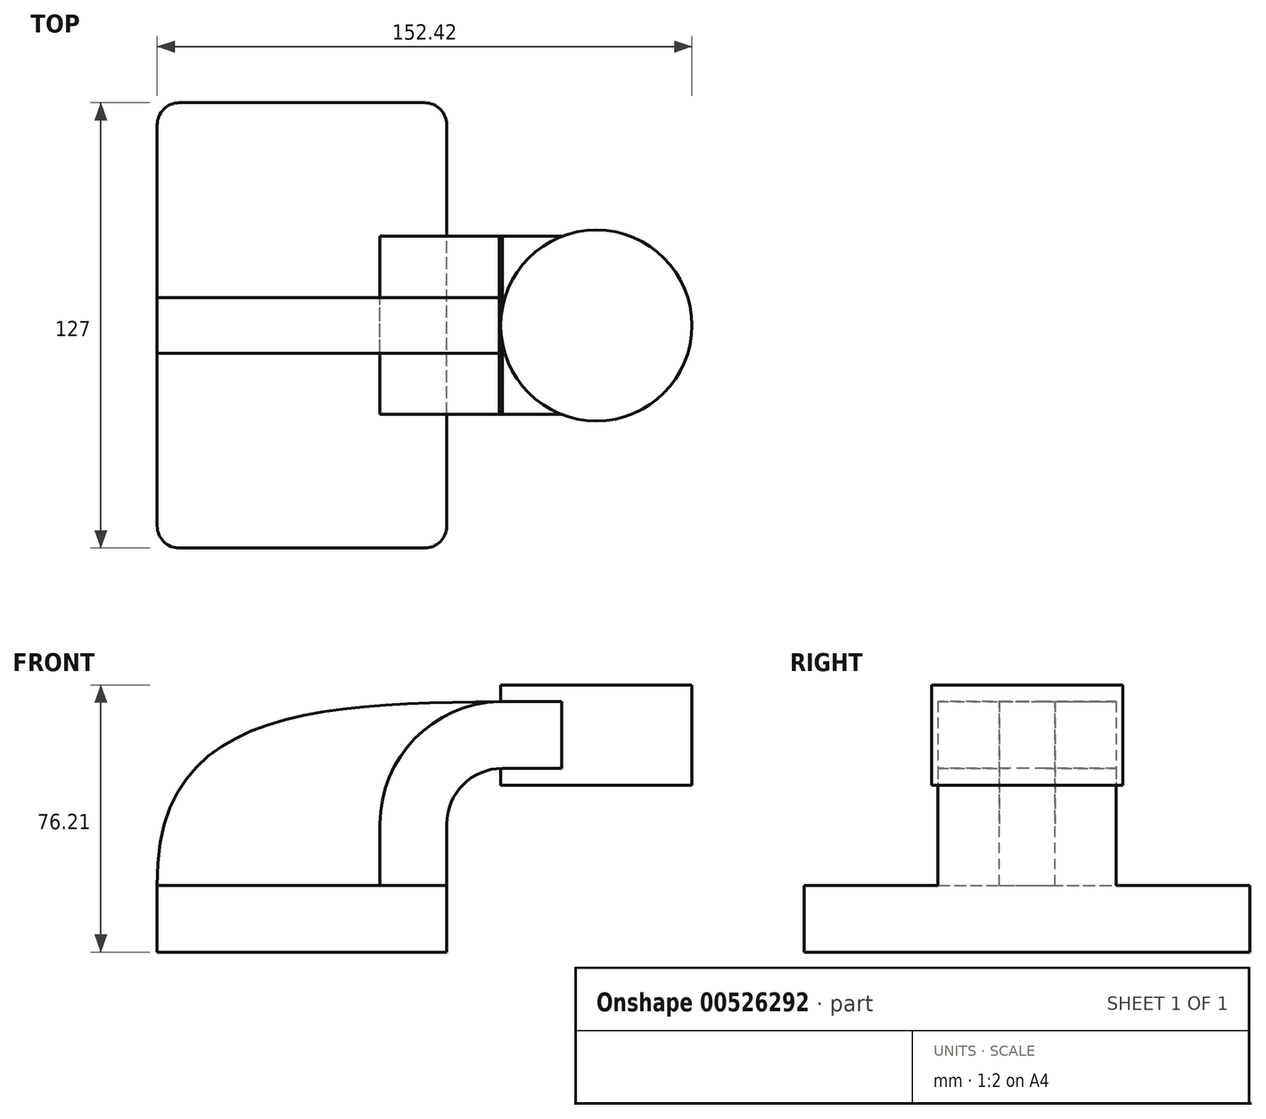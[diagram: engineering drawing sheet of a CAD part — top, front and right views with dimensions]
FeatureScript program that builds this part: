
annotation { "Feature Type Name" : "Feature", "Feature Type Description" : "" }
export const myFeature = defineFeature(function(context is Context, id is Id, definition is map)
    precondition{}
    {
        {
            var Q0;
            Q0=qCreatedBy(makeId("Front.planeOp"),FACE);
            var sketch = newSketch(context, id + "F0", { "sketchPlane" : qUnion([Q0])});
            skLineSegment(sketch, "E0.bottom", {"start": v(-41.28, 9.52) * mm, "end": v(41.27, 9.53) * mm});
            skLineSegment(sketch, "E0.top", {"start": v(-41.28, -9.52) * mm, "end": v(41.28, -9.52) * mm});
            skLineSegment(sketch, "E0.left", {"start": v(-41.28, 9.52) * mm, "end": v(-41.28, -9.53) * mm});
            skLineSegment(sketch, "E0.right", {"start": v(41.27, 9.53) * mm, "end": v(41.28, -9.52) * mm});
            skPoint(sketch, "E0.middle", {"position": v(0, 0) * mm});
            skLineSegment(sketch, "E1.bottom", {"start": v(60.32, 66.68) * mm, "end": v(111.12, 66.68) * mm});
            skLineSegment(sketch, "E1.top", {"start": v(60.33, 38.1) * mm, "end": v(111.12, 38.1) * mm});
            skLineSegment(sketch, "E1.left", {"start": v(60.32, 66.68) * mm, "end": v(60.33, 38.1) * mm});
            skLineSegment(sketch, "E1.right", {"start": v(111.12, 66.68) * mm, "end": v(111.12, 38.1) * mm});
            skPoint(sketch, "E1.middle", {"position": v(85.72, 52.39) * mm});
            skLineSegment(sketch, "E2", {"start": v(41.27, 9.53) * mm, "end": v(41.27, 27) * mm});
            skArc(sketch, "E3", {"start": v(41.27, 27) * mm, "mid": v(45.92, 38.23) * mm, "end": v(57.15, 42.88) * mm});
            skLineSegment(sketch, "E4", {"start": v(57.15, 42.88) * mm, "end": v(83.89, 42.88) * mm});
            skLineSegment(sketch, "E5.0", {"start": v(57.15, 61.93) * mm, "end": v(83.89, 61.93) * mm});
            skArc(sketch, "E5.1", {"start": v(22.22, 27) * mm, "mid": v(32.45, 51.7) * mm, "end": v(57.15, 61.93) * mm});
            skLineSegment(sketch, "E5.2", {"start": v(22.22, 9.53) * mm, "end": v(22.22, 27) * mm});
            skLineSegment(sketch, "E6", {"start": v(83.89, 38.1) * mm, "end": v(83.89, 66.68) * mm});
            skFitSpline(sketch, "E7", {"points": [v(-41.28, 9.52) * mm, v(57.15, 61.93) * mm], "startDerivative": vector(-2.54, 152.5) * mm, "endDerivative": vector(155.63, 2.18) * mm});
            skSolve(sketch);
        }
        {
            var Q0;
            Q0=makeQuery(id+"F0.imprint","IMPRINT",FACE,{"disambiguationData":[TD([[makeQuery(id+"F0.imprint","IMPRINT",EDGE,{"derivedFrom":sQuery(id+"F0.wireOp",EDGE,"E0.top")}),1.0]])]});
            extrude(context, id + "F1", {"entities" : qUnion([Q0]), "endBound" : BoundingType.SYMMETRIC, "depth" : 127 * mm, "offsetDistance" : 25.4 * mm});
        }
        {
            var Q0;
            {var subQ1=sQuery(id+"F0.wireOp",EDGE,"E2");Q0=makeQuery(id+"F0.imprint","IMPRINT",FACE,{"disambiguationData":[TD([[makeQuery(id+"F0.imprint","IMPRINT",EDGE,{"derivedFrom":subQ1}),1.0]])]});}
            var Q1;
            {var subQ0=sQuery(id+"F0.wireOp",EDGE,"E5.0");var subQ1=sQuery(id+"F0.wireOp",EDGE,"E1.left");var subQ2=makeQuery(id+"F0.imprint","INTERSECT",VERTEX,{"derivedFrom":[subQ1,subQ0]});Q1=makeQuery(id+"F0.imprint","IMPRINT",FACE,{"disambiguationData":[TD([[makeQuery(id+"F0.imprint","IMPRINT",EDGE,{"disambiguationData":[TD([[subQ2,-1.0]])],"derivedFrom":subQ1}),1.0]])]});}
            extrude(context, id + "F2", {"entities" : qUnion([Q0, Q1]), "operationType" : NewBodyOperationType.ADD, "endBound" : BoundingType.SYMMETRIC, "depth" : 50.8 * mm, "offsetDistance" : 25.4 * mm});
        }
        {
            var Q0;
            {var subQ3=sQuery(id+"F0.wireOp",EDGE,"E5.2");Q0=makeQuery(id+"F0.imprint","IMPRINT",FACE,{"disambiguationData":[TD([[makeQuery(id+"F0.imprint","IMPRINT",EDGE,{"derivedFrom":subQ3}),1.0]])]});}
            extrude(context, id + "F3", {"entities" : qUnion([Q0]), "endBound" : BoundingType.SYMMETRIC, "depth" : 15.88 * mm, "offsetDistance" : 25.4 * mm});
        }
        {
            var Q0;
            {var subQ4=sQuery(id+"F0.wireOp",EDGE,"E1.right");Q0=makeQuery(id+"F0.imprint","IMPRINT",FACE,{"disambiguationData":[TD([[makeQuery(id+"F0.imprint","IMPRINT",EDGE,{"derivedFrom":subQ4}),-1.0]])]});}
            var Q1;
            Q1=sQuery(id+"F0.wireOp",EDGE,"E6");
            revolve(context, id + "F4", {"operationType" : NewBodyOperationType.ADD, "entities" : qUnion([Q0]), "axis" : qUnion([Q1]), "revolveType" : RevolveType.FULL});
        }
        {
            var Q0;
            Q0=makeQuery(id+"F1.opExtrude","CAP_EDGE",EDGE,{"disambiguationData":[OSD([sQuery(id+"F0.wireOp",EDGE,"E0.left")])],"isStart":false});
            var Q1;
            Q1=makeQuery(id+"F1.opExtrude","CAP_EDGE",EDGE,{"disambiguationData":[OSD([sQuery(id+"F0.wireOp",EDGE,"E0.right")])],"isStart":false});
            var Q2;
            Q2=makeQuery(id+"F1.opExtrude","CAP_EDGE",EDGE,{"disambiguationData":[OSD([sQuery(id+"F0.wireOp",EDGE,"E0.right")])],"isStart":true});
            var Q3;
            Q3=makeQuery(id+"F1.opExtrude","CAP_EDGE",EDGE,{"disambiguationData":[OSD([sQuery(id+"F0.wireOp",EDGE,"E0.left")])],"isStart":true});
            fillet(context, id + "F5", {"entities" : qUnion([Q0, Q1, Q2, Q3]), "radius" : 6.35 * mm, "tangentPropagation" : true, "allowEdgeOverflow" : false});
        }
    });
